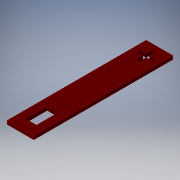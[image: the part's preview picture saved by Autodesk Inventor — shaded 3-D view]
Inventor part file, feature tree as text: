
AUTODESK INVENTOR PART (.ipt)
format: ipt  version: 2019 (Build 230136000, 136)  size: 132,608 bytes
history: native  units: mm
features: extrude x1, sketch x1
ambient origin geometry x8: Origin, YZ Plane, XZ Plane, XY Plane, X Axis, Y Axis, Z Axis, Center Point
bodies: Body1 (feature_tree)
feature tree (2):
  extrude  "Extrusion3"  Depth=20.0mm
  sketch  "Sketch1"  dims[d24=10.0mm d25=20.0mm d26=25.0mm d27=130.0mm d28=20.0mm d29=12.5mm d37=3.18mm d38=15.0mm d39=15.0mm d40=3.18mm d41=12.5mm d42=12.5mm d43=3.18mm d44=0.0mm]
